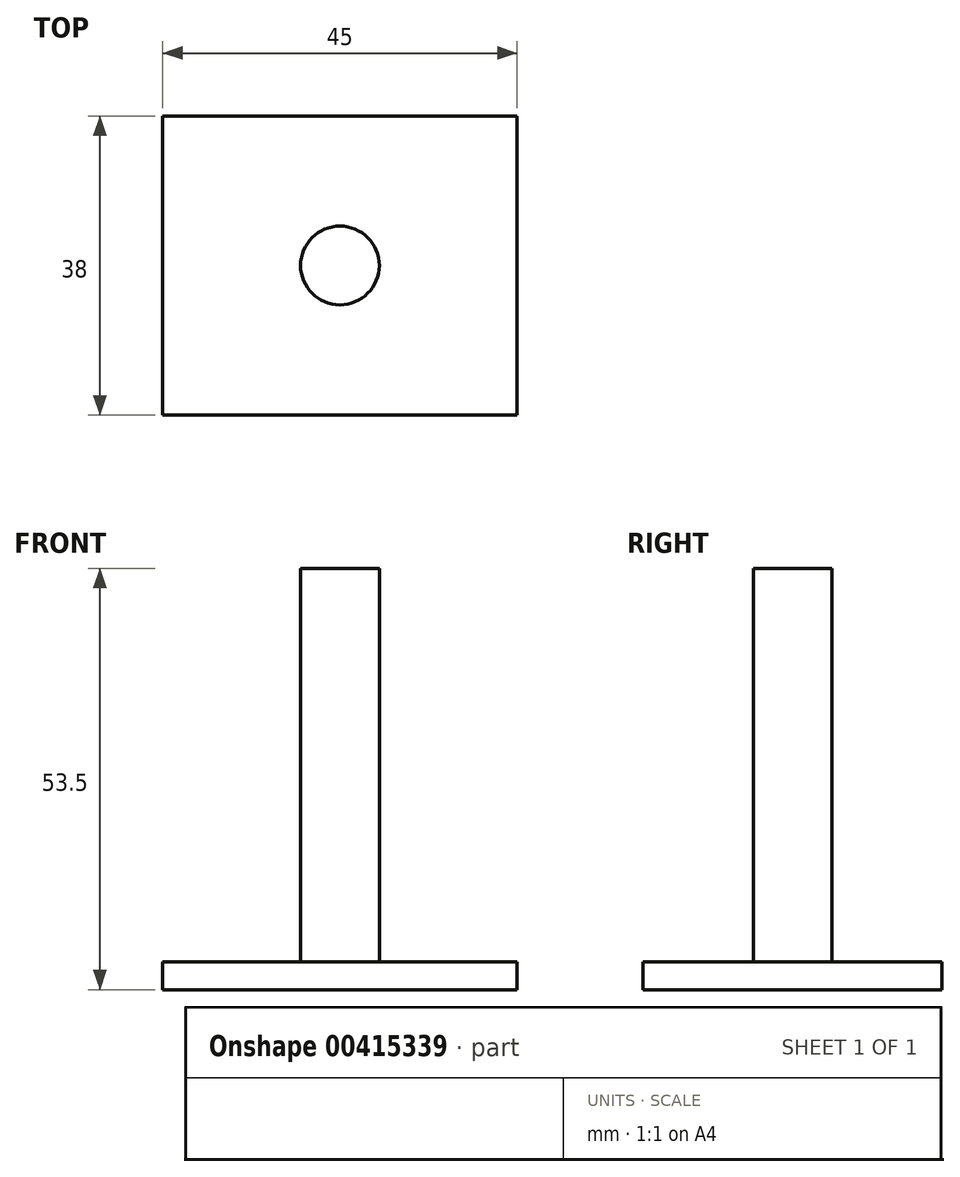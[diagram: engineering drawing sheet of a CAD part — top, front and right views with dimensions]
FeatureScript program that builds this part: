
annotation { "Feature Type Name" : "Feature", "Feature Type Description" : "" }
export const myFeature = defineFeature(function(context is Context, id is Id, definition is map)
    precondition{}
    {
        {
            var Q0;
            Q0=qCreatedBy(makeId("Top.planeOp"),FACE);
            var sketch = newSketch(context, id + "F0", { "sketchPlane" : qUnion([Q0])});
            skLineSegment(sketch, "E0.bottom", {"start": v(-22.5, 19) * mm, "end": v(22.5, 19) * mm});
            skLineSegment(sketch, "E0.top", {"start": v(-22.5, -19) * mm, "end": v(22.5, -19) * mm});
            skLineSegment(sketch, "E0.left", {"start": v(-22.5, 19) * mm, "end": v(-22.5, -19) * mm});
            skLineSegment(sketch, "E0.right", {"start": v(22.5, 19) * mm, "end": v(22.5, -19) * mm});
            skPoint(sketch, "E0.middle", {"position": v(0, 0) * mm});
            skSolve(sketch);
        }
        {
            var Q0;
            Q0 = qSketchRegion(id + "F0", true);
            extrude(context, id + "F1", {"entities" : qUnion([Q0]), "oppositeDirection" : true, "depth" : 3.5 * mm});
        }
        {
            var Q0;
            Q0=makeQuery(id+"F1.opExtrude","CAP_FACE",FACE,{"disambiguationData":[OSD([sQuery(id+"F0.wireOp",EDGE,"E0.bottom"),sQuery(id+"F0.wireOp",EDGE,"E0.top"),sQuery(id+"F0.wireOp",EDGE,"E0.left"),sQuery(id+"F0.wireOp",EDGE,"E0.right")])],"isStart":true});
            var sketch = newSketch(context, id + "F2", { "sketchPlane" : qUnion([Q0])});
            skCircle(sketch, "E1", {"center": v(0, 0) * mm, "radius": 5 * mm});
            skSolve(sketch);
        }
        {
            var Q0;
            Q0 = qSketchRegion(id + "F2", true);
            extrude(context, id + "F3", {"entities" : qUnion([Q0]), "operationType" : NewBodyOperationType.ADD, "depth" : 50 * mm});
        }
    });
